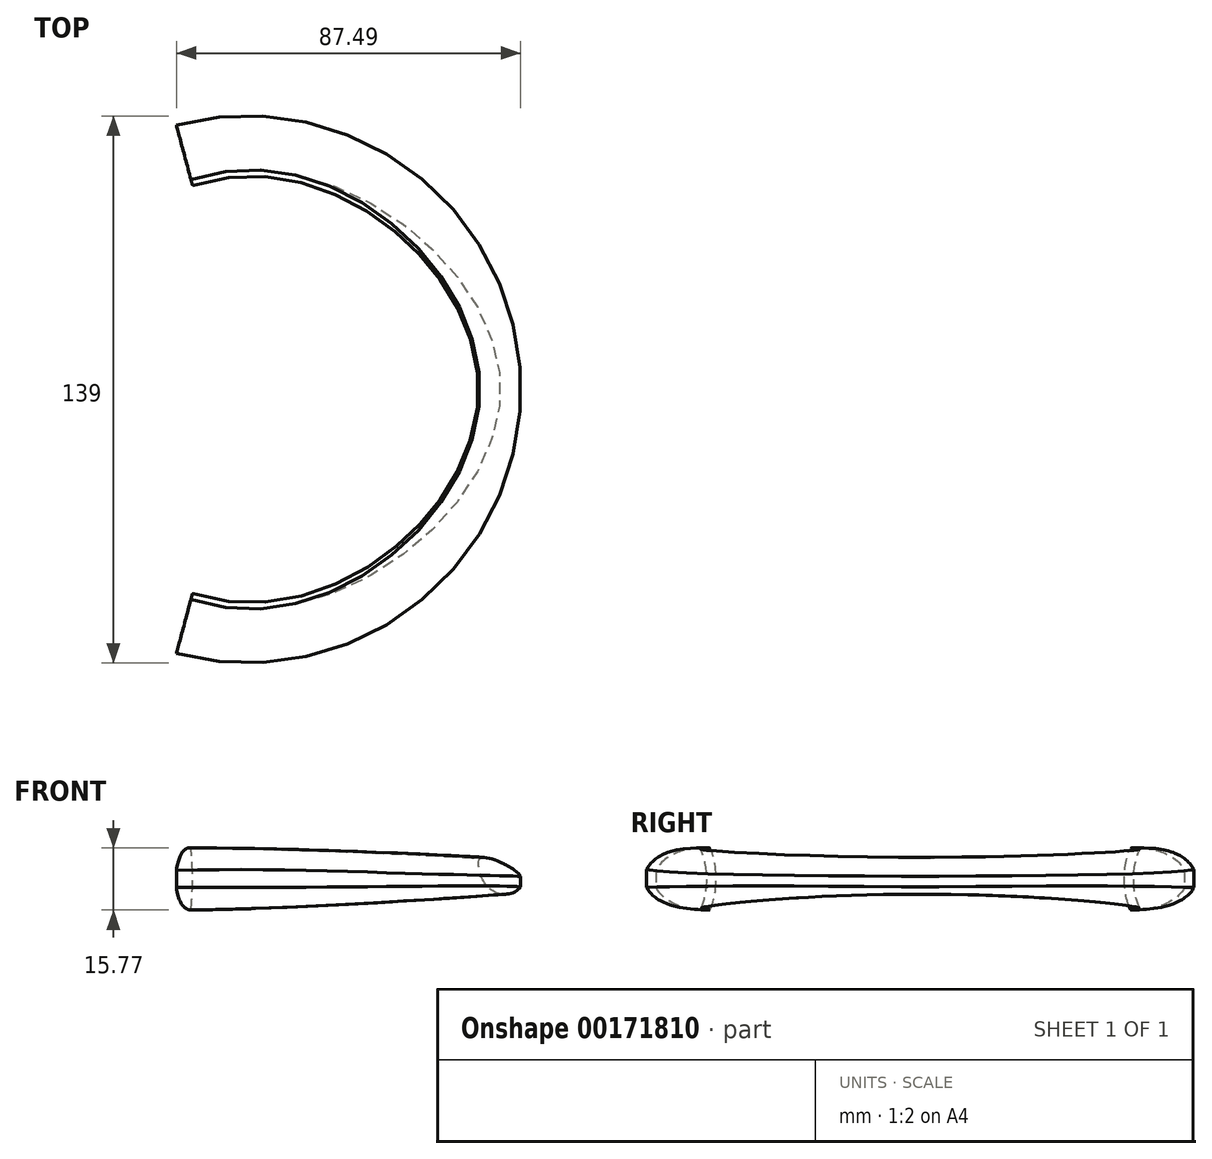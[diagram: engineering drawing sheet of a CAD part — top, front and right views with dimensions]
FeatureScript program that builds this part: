
annotation { "Feature Type Name" : "Feature", "Feature Type Description" : "" }
export const myFeature = defineFeature(function(context is Context, id is Id, definition is map)
    precondition{}
    {
        {
            var Q0;
            Q0=qCreatedBy(makeId("Top.planeOp"),FACE);
            var sketch = newSketch(context, id + "F0", { "sketchPlane" : qUnion([Q0])});
            skCircle(sketch, "E0", {"center": v(0, 0) * mm, "radius": 70 * mm});
            skLineSegment(sketch, "E1", {"start": v(-3.54, -3.54) * mm, "end": v(3.54, 3.54) * mm});
            skLineSegment(sketch, "E2", {"start": v(3.54, -3.54) * mm, "end": v(-3.54, 3.54) * mm});
            skCircle(sketch, "E3", {"center": v(0, 0) * mm, "radius": 60 * mm, "construction": true});
            skCircle(sketch, "E4", {"center": v(0, 0) * mm, "radius": 65 * mm});
            skSolve(sketch);
        }
        {
            var Q0;
            Q0=qCreatedBy(makeId("Front.planeOp"),FACE);
            var sketch = newSketch(context, id + "F1", { "sketchPlane" : qUnion([Q0])});
            skFitSpline(sketch, "E5", {"points": [v(-56.9, -7.15) * mm, v(-56.84, 8.05) * mm], "startDerivative": vector(7.12, 14.12) * mm, "endDerivative": vector(-5.74, 12.11) * mm});
            skFitSpline(sketch, "E6", {"points": [v(-56.9, -7.15) * mm, v(-56.84, 8.05) * mm], "startDerivative": vector(-52.06, -1.38) * mm, "endDerivative": vector(53.02, 1.4) * mm});
            skPoint(sketch, "E7", {"position": v(-70, 0) * mm});
            skFitSpline(sketch, "E8", {"points": [v(59.12, 5.77) * mm, v(64.3, -3.3) * mm], "startDerivative": vector(-3.05, -2.68) * mm, "endDerivative": vector(15.46, -2.9) * mm});
            skFitSpline(sketch, "E9", {"points": [v(64.3, -3.3) * mm, v(70, 0) * mm], "startDerivative": vector(11.49, -1.46) * mm, "endDerivative": vector(-0.19, 4.31) * mm});
            skFitSpline(sketch, "E10", {"points": [v(70, 0) * mm, v(59.12, 5.77) * mm], "startDerivative": vector(-0.61, 9) * mm, "endDerivative": vector(-4.09, -3.42) * mm});
            skFitSpline(sketch, "E11.MirrorCS", {"points": [v(56.9, -7.15) * mm, v(56.84, 8.05) * mm], "startDerivative": vector(-7.12, 14.12) * mm, "endDerivative": vector(5.74, 12.11) * mm, "construction": true});
            skFitSpline(sketch, "E12.MirrorCS", {"points": [v(56.9, -7.15) * mm, v(56.84, 8.05) * mm], "startDerivative": vector(52.06, -1.38) * mm, "endDerivative": vector(-53.02, 1.4) * mm, "construction": true});
            skSolve(sketch);
        }
        {
            var Q0;
            Q0=qCreatedBy(makeId("Right.planeOp"),FACE);
            var sketch = newSketch(context, id + "F2", { "sketchPlane" : qUnion([Q0])});
            skFitSpline(sketch, "E13", {"points": [v(-55.8, -7.07) * mm, v(-55.8, 8.13) * mm], "startDerivative": vector(7.12, 14.12) * mm, "endDerivative": vector(-5.74, 12.11) * mm});
            skFitSpline(sketch, "E14", {"points": [v(-55.8, -7.07) * mm, v(-55.8, 8.13) * mm], "startDerivative": vector(-62.47, 0.08) * mm, "endDerivative": vector(51.06, -5.02) * mm});
            skPoint(sketch, "E15", {"position": v(-70, 0) * mm});
            skFitSpline(sketch, "E16.MirrorCS", {"points": [v(55.8, -7.07) * mm, v(55.8, 8.13) * mm], "startDerivative": vector(-7.12, 14.12) * mm, "endDerivative": vector(5.74, 12.11) * mm});
            skPoint(sketch, "E17.MirrorP", {"position": v(70, 0) * mm});
            skFitSpline(sketch, "E18.MirrorCS", {"points": [v(55.8, -7.07) * mm, v(55.8, 8.13) * mm], "startDerivative": vector(62.47, 0.08) * mm, "endDerivative": vector(-51.06, -5.02) * mm});
            skPoint(sketch, "E19.middle", {"position": v(-65, 0) * mm});
            skSolve(sketch);
        }
        {
            var Q0;
            Q0=makeQuery(id+"F2.imprint","IMPRINT",FACE,{"disambiguationData":[TD([[makeQuery(id+"F2.imprint","IMPRINT",EDGE,{"derivedFrom":sQuery(id+"F2.wireOp",EDGE,"E16.MirrorCS")}),-1.0]])]});
            var Q1;
            Q1=makeQuery(id+"F1.imprint","IMPRINT",FACE,{"disambiguationData":[TD([[makeQuery(id+"F1.imprint","IMPRINT",EDGE,{"derivedFrom":sQuery(id+"F1.wireOp",EDGE,"E8")}),1.0]])]});
            var Q2;
            Q2=makeQuery(id+"F2.imprint","IMPRINT",FACE,{"disambiguationData":[TD([[makeQuery(id+"F2.imprint","IMPRINT",EDGE,{"derivedFrom":sQuery(id+"F2.wireOp",EDGE,"E13")}),1.0]])]});
            var Q3;
            Q3=makeQuery(id+"F1.imprint","IMPRINT",FACE,{"disambiguationData":[TD([[makeQuery(id+"F1.imprint","IMPRINT",EDGE,{"derivedFrom":sQuery(id+"F1.wireOp",EDGE,"E5")}),1.0]])]});
            var Q4;
            Q4=sQuery(id+"F0.wireOp",EDGE,"E0");
            loft(context, id + "F3", {"addGuides" : true, "sheetProfilesArray" : [{ "sheetProfileEntities" : qUnion([Q0]) }, { "sheetProfileEntities" : qUnion([Q1]) }, { "sheetProfileEntities" : qUnion([Q2]) }, { "sheetProfileEntities" : qUnion([Q3]) }], "guidesArray" : [{ "guideEntities" : qUnion([Q4]), "guideDerivativeType" : LoftGuideDerivativeType.DEFAULT, "guideDerivativeMagnitude" : 1 }]});
        }
        {
            var Q0;
            Q0=qCreatedBy(makeId("Top.planeOp"),FACE);
            var sketch = newSketch(context, id + "F4", { "sketchPlane" : qUnion([Q0])});
            skLineSegment(sketch, "E20", {"start": v(0, 0) * mm, "end": v(-44.61, 0) * mm, "construction": true});
            skLineSegment(sketch, "E21", {"start": v(0, 0) * mm, "end": v(-1538.46, 5741.6) * mm});
            skLineSegment(sketch, "E22.MirrorCS", {"start": v(0, 0) * mm, "end": v(-1538.46, -5741.6) * mm});
            skLineSegment(sketch, "E23", {"start": v(-1538.46, 5741.6) * mm, "end": v(-1538.46, -5741.6) * mm});
            skLineSegment(sketch, "E24", {"start": v(-1538.46, -5741.6) * mm, "end": v(-1538.46, -5741.6) * mm});
            skSolve(sketch);
        }
        {
            var Q0;
            Q0 = qSketchRegion(id + "F4", true);
            extrude(context, id + "F5", {"entities" : qUnion([Q0]), "operationType" : NewBodyOperationType.REMOVE, "oppositeDirection" : true, "depth" : 10 * mm, "hasSecondDirection" : true, "secondDirectionOppositeDirection" : false, "secondDirectionDepth" : 10 * mm});
        }
        {
            var Q0;
            Q0=qCreatedBy(makeId("Top.planeOp"),FACE);
            var sketch = newSketch(context, id + "F6", { "sketchPlane" : qUnion([Q0])});
            skCircle(sketch, "E25", {"center": v(0, 0) * mm, "radius": 69.5 * mm});
            skSolve(sketch);
        }
        {
            var Q0;
            Q0 = qSketchRegion(id + "F6", true);
            extrude(context, id + "F7", {"entities" : qUnion([Q0]), "operationType" : NewBodyOperationType.INTERSECT, "depth" : 25 * mm, "hasSecondDirection" : true, "secondDirectionOppositeDirection" : true, "secondDirectionDepth" : 25 * mm});
        }
    });
